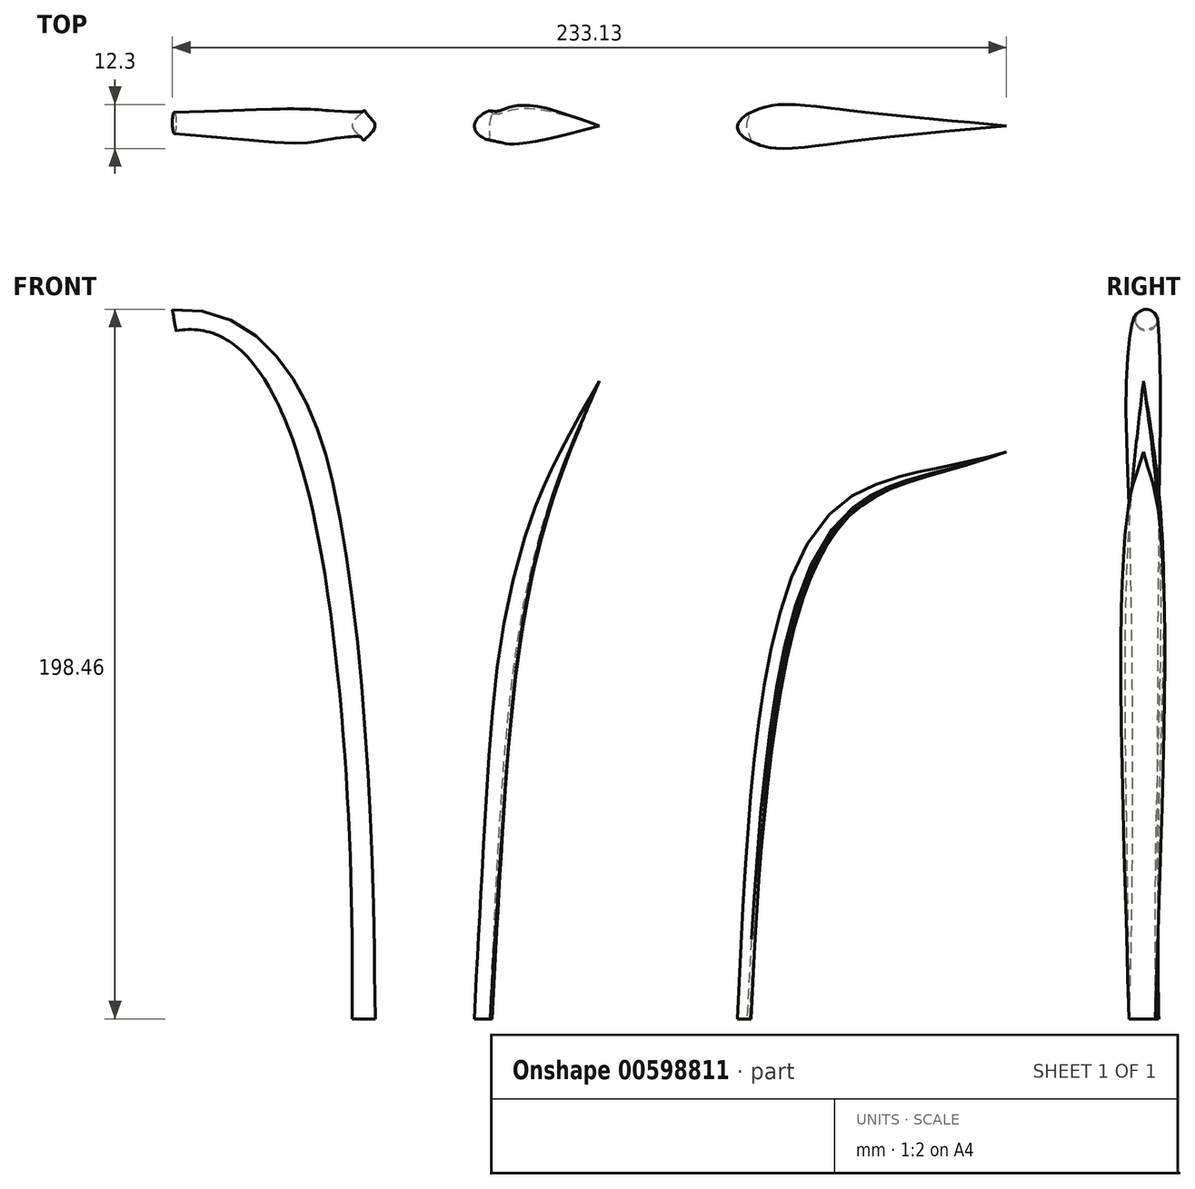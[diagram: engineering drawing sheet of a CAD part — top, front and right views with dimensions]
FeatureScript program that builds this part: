
annotation { "Feature Type Name" : "Feature", "Feature Type Description" : "" }
export const myFeature = defineFeature(function(context is Context, id is Id, definition is map)
    precondition{}
    {
        {
            var Q0;
            Q0=qCreatedBy(makeId("Front.planeOp"),FACE);
            var sketch = newSketch(context, id + "F0", { "sketchPlane" : qUnion([Q0])});
            skFitSpline(sketch, "E0", {"points": [v(0, 0) * mm, v(-2.83, 82.9) * mm, v(-49.28, 192.55) * mm], "startDerivative": vector(-0.72, 79.2) * mm, "endDerivative": vector(-178, -31.1) * mm});
            skFitSpline(sketch, "E1", {"points": [v(38.29, 0) * mm, v(69.02, 178.35) * mm], "startDerivative": vector(3.32, 285.1) * mm, "endDerivative": vector(50.55, 74.56) * mm});
            skPoint(sketch, "E2", {"position": v(40.67, 57.92) * mm});
            skPoint(sketch, "E3", {"position": v(54.64, 145.1) * mm});
            skPoint(sketch, "E4", {"position": v(-9.9, 136.52) * mm});
            skFitSpline(sketch, "E5", {"points": [v(110.32, 0) * mm, v(137.72, 141) * mm, v(182.84, 158.6) * mm], "startDerivative": vector(18.34, 346.3) * mm, "endDerivative": vector(148.53, 53.4) * mm});
            skPoint(sketch, "E6", {"position": v(-26, 181.05) * mm});
            skSolve(sketch);
        }
        {
            var Q0;
            Q0=qCreatedBy(makeId("Top.planeOp"),FACE);
            var sketch = newSketch(context, id + "F1", { "sketchPlane" : qUnion([Q0])});
            skFitSpline(sketch, "E7", {"points": [v(4.18, 3.21) * mm, v(3.4, 4.3) * mm, v(2.35, 3.35) * mm, v(0, 0) * mm, v(2.53, -3.35) * mm, v(3.17, -4.05) * mm, v(4, -3.3) * mm, v(6.4, 0) * mm, v(4.18, 3.21) * mm]});
            skFitSpline(sketch, "E8", {"points": [v(38.78, 4.18) * mm, v(34.1, 0) * mm, v(38.12, -3.82) * mm, v(38.4, 0) * mm, v(38.78, 4.18) * mm]});
            skFitSpline(sketch, "E9", {"points": [v(107.7, -0.43) * mm, v(111.34, -4.07) * mm, v(110.32, 0) * mm, v(111, 3.37) * mm, v(107.7, -0.43) * mm]});
            skSolve(sketch);
        }
        {
            var Q0;
            Q0=sQuery(id+"F0.wireOp",EDGE,"E0");
            var Q1;
            Q1=sQuery(id+"F0.wireOp",VERTEX,"E0.2.internal");
            cPlane(context, id + "F2", {"entities" : qUnion([Q0, Q1]), "cplaneType" : CPlaneType.CURVE_POINT, "offset" : 25 * mm, "width" : 150 * mm, "height" : 150 * mm});
        }
        {
            var Q0;
            Q0=qCreatedBy(id+"F2.planeOp",FACE);
            var sketch = newSketch(context, id + "F3", { "sketchPlane" : qUnion([Q0])});
            skCircle(sketch, "E10", {"center": v(-0.83, 201.04) * mm, "radius": 3 * mm});
            skPoint(sketch, "E11", {"position": v(0, -75.34) * mm});
            skPoint(sketch, "E12", {"position": v(0, 198.16) * mm});
            skPoint(sketch, "E13", {"position": v(-3.62, 199.95) * mm});
            skPoint(sketch, "E14", {"position": v(-3.83, 201) * mm});
            skPoint(sketch, "E15", {"position": v(-3.52, 202.37) * mm});
            skPoint(sketch, "E16", {"position": v(2.05, 201.89) * mm});
            skPoint(sketch, "E17", {"position": v(2.1, 207.18) * mm});
            skPoint(sketch, "E18", {"position": v(1.8, 206.21) * mm});
            skSolve(sketch);
        }
        {
            var Q0;
            Q0=sQuery(id+"F0.wireOp",VERTEX,"E4");
            var Q1;
            Q1=sQuery(id+"F0.wireOp",EDGE,"E0");
            cPlane(context, id + "F4", {"entities" : qUnion([Q0, Q1]), "cplaneType" : CPlaneType.CURVE_POINT, "offset" : 25 * mm, "width" : 150 * mm, "height" : 150 * mm});
        }
        {
            var Q0;
            Q0=qCreatedBy(id+"F4.planeOp",FACE);
            var sketch = newSketch(context, id + "F5", { "sketchPlane" : qUnion([Q0])});
            skFitSpline(sketch, "E19", {"points": [v(22.32, 2.94) * mm, v(20.83, 4.27) * mm, v(20.03, 3.65) * mm, v(17.36, 0) * mm, v(19.77, -3.19) * mm, v(20.64, -3.84) * mm, v(21.71, -3.23) * mm, v(24.36, 0) * mm, v(22.32, 2.94) * mm]});
            skSolve(sketch);
        }
        {
            var Q0;
            Q0=sQuery(id+"F0.wireOp",VERTEX,"E2");
            var Q1;
            Q1=sQuery(id+"F0.wireOp",EDGE,"E1");
            cPlane(context, id + "F6", {"entities" : qUnion([Q0, Q1]), "cplaneType" : CPlaneType.CURVE_POINT, "offset" : 25 * mm, "width" : 150 * mm, "height" : 150 * mm});
        }
        {
            var Q0;
            Q0=sQuery(id+"F0.wireOp",VERTEX,"E3");
            var Q1;
            Q1=sQuery(id+"F0.wireOp",EDGE,"E1");
            cPlane(context, id + "F7", {"entities" : qUnion([Q0, Q1]), "cplaneType" : CPlaneType.CURVE_POINT, "offset" : 25 * mm, "width" : 150 * mm, "height" : 150 * mm});
        }
        {
            var Q0;
            Q0=qCreatedBy(id+"F6.planeOp",FACE);
            var sketch = newSketch(context, id + "F8", { "sketchPlane" : qUnion([Q0])});
            skFitSpline(sketch, "E20", {"points": [v(37.78, 4.33) * mm, v(32.78, 0) * mm, v(37.65, -4.7) * mm, v(36.88, 0) * mm, v(37.78, 4.33) * mm]});
            skSolve(sketch);
        }
        {
            var Q0;
            Q0=qCreatedBy(id+"F7.planeOp",FACE);
            var sketch = newSketch(context, id + "F9", { "sketchPlane" : qUnion([Q0])});
            skFitSpline(sketch, "E21", {"points": [v(12.54, 4.51) * mm, v(9, 0.37) * mm, v(12.24, -3.49) * mm, v(12.2, 0) * mm, v(12.54, 4.51) * mm]});
            skSolve(sketch);
        }
        {
            var Q0;
            Q0=sQuery(id+"F0.wireOp",VERTEX,"E6");
            var Q1;
            Q1=sQuery(id+"F0.wireOp",EDGE,"E0");
            cPlane(context, id + "F10", {"entities" : qUnion([Q0, Q1]), "cplaneType" : CPlaneType.CURVE_POINT, "offset" : 25 * mm, "width" : 150 * mm, "height" : 150 * mm});
        }
        {
            var Q0;
            Q0=qCreatedBy(id+"F10.planeOp",FACE);
            var sketch = newSketch(context, id + "F11", { "sketchPlane" : qUnion([Q0])});
            skPoint(sketch, "E22.0", {"position": v(83.51, 0) * mm});
            skFitSpline(sketch, "E23", {"points": [v(83.51, 0) * mm, v(85.67, -3.54) * mm, v(86.94, -4.5) * mm, v(90.01, 0.2) * mm, v(87.85, 3.49) * mm, v(86.56, 4.64) * mm, v(85.87, 3.72) * mm, v(83.51, 0) * mm]});
            skSolve(sketch);
        }
        {
            var Q0;
            Q0=makeQuery(id+"F1.imprint","IMPRINT",FACE,{"disambiguationData":[TD([[makeQuery(id+"F1.imprint","IMPRINT",EDGE,{"derivedFrom":sQuery(id+"F1.wireOp",EDGE,"E8")}),1.0]])]});
            var Q1;
            Q1=makeQuery(id+"F8.imprint","IMPRINT",FACE,{"disambiguationData":[TD([[makeQuery(id+"F8.imprint","IMPRINT",EDGE,{"derivedFrom":sQuery(id+"F8.wireOp",EDGE,"E20")}),1.0]])]});
            var Q2;
            Q2=makeQuery(id+"F9.imprint","IMPRINT",FACE,{"disambiguationData":[TD([[makeQuery(id+"F9.imprint","IMPRINT",EDGE,{"derivedFrom":sQuery(id+"F9.wireOp",EDGE,"E21")}),1.0]])]});
            var Q3;
            Q3=sQuery(id+"F0.wireOp",VERTEX,"E1.1.internal");
            loft(context, id + "F12", {"sheetProfilesArray" : [{ "sheetProfileEntities" : qUnion([Q0]) }, { "sheetProfileEntities" : qUnion([Q1]) }, { "sheetProfileEntities" : qUnion([Q2]) }, { "sheetProfileEntities" : qUnion([Q3]) }]});
        }
        {
            var Q0;
            Q0=makeQuery(id+"F1.imprint","IMPRINT",FACE,{"disambiguationData":[TD([[makeQuery(id+"F1.imprint","IMPRINT",EDGE,{"derivedFrom":sQuery(id+"F1.wireOp",EDGE,"E7")}),1.0]])]});
            var Q1;
            Q1=makeQuery(id+"F5.imprint","IMPRINT",FACE,{"disambiguationData":[TD([[makeQuery(id+"F5.imprint","IMPRINT",EDGE,{"derivedFrom":sQuery(id+"F5.wireOp",EDGE,"E19")}),1.0]])]});
            var Q2;
            Q2=makeQuery(id+"F11.imprint","IMPRINT",FACE,{"disambiguationData":[TD([[makeQuery(id+"F11.imprint","IMPRINT",EDGE,{"derivedFrom":sQuery(id+"F11.wireOp",EDGE,"E23")}),1.0]])]});
            var Q3;
            Q3=makeQuery(id+"F3.imprint","IMPRINT",FACE,{"disambiguationData":[TD([[makeQuery(id+"F3.imprint","IMPRINT",EDGE,{"derivedFrom":sQuery(id+"F3.wireOp",EDGE,"E10")}),1.0]])]});
            var Q4;
            Q4=sQuery(id+"F0.wireOp",EDGE,"E0");
            loft(context, id + "F13", {"addGuides" : true, "sheetProfilesArray" : [{ "sheetProfileEntities" : qUnion([Q0]) }, { "sheetProfileEntities" : qUnion([Q1]) }, { "sheetProfileEntities" : qUnion([Q2]) }, { "sheetProfileEntities" : qUnion([Q3]) }], "guidesArray" : [{ "guideEntities" : qUnion([Q4]), "guideDerivativeType" : LoftGuideDerivativeType.DEFAULT, "guideDerivativeMagnitude" : 1 }]});
        }
        {
            var Q0;
            Q0=sQuery(id+"F0.wireOp",VERTEX,"E5.1.internal");
            var Q1;
            Q1=sQuery(id+"F0.wireOp",EDGE,"E5");
            cPlane(context, id + "F14", {"entities" : qUnion([Q0, Q1]), "cplaneType" : CPlaneType.CURVE_POINT, "offset" : 25 * mm, "width" : 150 * mm, "height" : 150 * mm});
        }
        {
            var Q0;
            Q0=qCreatedBy(id+"F14.planeOp",FACE);
            var sketch = newSketch(context, id + "F15", { "sketchPlane" : qUnion([Q0])});
            skPoint(sketch, "E24.0", {"position": v(0, 4.8) * mm});
            skFitSpline(sketch, "E25", {"points": [v(0, 4.8) * mm, v(4.34, 3.78) * mm, v(0, 7.87) * mm, v(-4.52, 4.53) * mm, v(0, 4.8) * mm]});
            skSolve(sketch);
        }
        {
            var Q0;
            Q0=makeQuery(id+"F1.imprint","IMPRINT",FACE,{"disambiguationData":[TD([[makeQuery(id+"F1.imprint","IMPRINT",EDGE,{"derivedFrom":sQuery(id+"F1.wireOp",EDGE,"E9")}),1.0]])]});
            var Q1;
            Q1=makeQuery(id+"F15.imprint","IMPRINT",FACE,{"disambiguationData":[TD([[makeQuery(id+"F15.imprint","IMPRINT",EDGE,{"derivedFrom":sQuery(id+"F15.wireOp",EDGE,"E25")}),1.0]])]});
            var Q2;
            Q2=sQuery(id+"F0.wireOp",VERTEX,"E5.end");
            var Q3;
            Q3=sQuery(id+"F0.wireOp",EDGE,"E5");
            loft(context, id + "F16", {"addGuides" : true, "sheetProfilesArray" : [{ "sheetProfileEntities" : qUnion([Q0]) }, { "sheetProfileEntities" : qUnion([Q1]) }, { "sheetProfileEntities" : qUnion([Q2]) }], "guidesArray" : [{ "guideEntities" : qUnion([Q3]), "guideDerivativeType" : LoftGuideDerivativeType.DEFAULT, "guideDerivativeMagnitude" : 1 }]});
        }
    });
